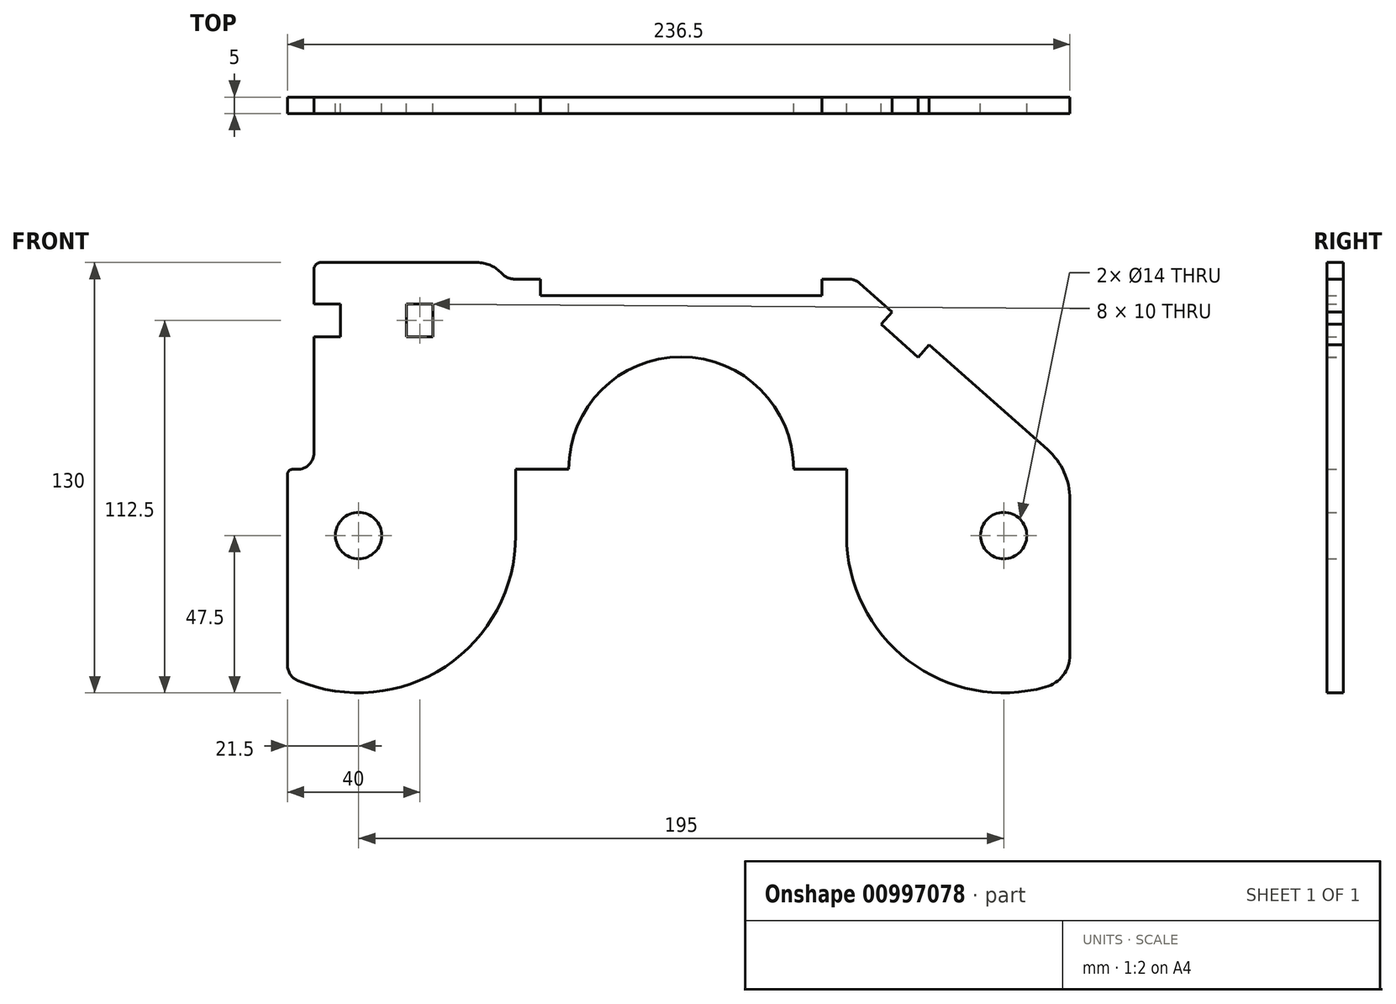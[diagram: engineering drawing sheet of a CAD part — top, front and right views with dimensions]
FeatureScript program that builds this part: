
annotation { "Feature Type Name" : "Feature", "Feature Type Description" : "" }
export const myFeature = defineFeature(function(context is Context, id is Id, definition is map)
    precondition{}
    {
        {
            var Q0;
            Q0=qCreatedBy(makeId("Front.planeOp"),FACE);
            var sketch = newSketch(context, id + "F0", { "sketchPlane" : qUnion([Q0])});
            skCircle(sketch, "E0", {"center": v(-97.5, -20) * mm, "radius": 7 * mm});
            skCircle(sketch, "E1", {"center": v(97.5, -20) * mm, "radius": 7 * mm});
            skArc(sketch, "E2", {"start": v(34, 0) * mm, "mid": v(0, 34) * mm, "end": v(-34, 0) * mm});
            skLineSegment(sketch, "E3", {"start": v(117.5, -9.01) * mm, "end": v(117.5, -56.14) * mm});
            skPoint(sketch, "E4.visualSharp", {"position": v(-34, 0) * mm});
            skPoint(sketch, "E5.visualSharp", {"position": v(34, 0) * mm});
            skPoint(sketch, "E6.visualSharp", {"position": v(117.5, 57.5) * mm});
            skLineSegment(sketch, "E7", {"start": v(-184.02, 45) * mm, "end": v(157.58, 45) * mm, "construction": true});
            skArc(sketch, "E8", {"start": v(-115.94, -63.77) * mm, "mid": v(-71.23, -59.57) * mm, "end": v(-50, -20) * mm});
            skArc(sketch, "E9", {"start": v(50, -20) * mm, "mid": v(68.74, -57.8) * mm, "end": v(110.17, -65.78) * mm});
            skLineSegment(sketch, "E10", {"start": v(-111, 60.5) * mm, "end": v(-111, 50) * mm});
            skPoint(sketch, "E11.visualSharp", {"position": v(-111, 0) * mm});
            skPoint(sketch, "E12.visualSharp", {"position": v(-111, 62.5) * mm});
            skLineSegment(sketch, "E13.bottom", {"start": v(-111, 50) * mm, "end": v(-103, 50) * mm});
            skLineSegment(sketch, "E13.top", {"start": v(-111, 40) * mm, "end": v(-103, 40) * mm});
            skLineSegment(sketch, "E13.right", {"start": v(-103, 50) * mm, "end": v(-103, 40) * mm});
            skLineSegment(sketch, "E14.bottom", {"start": v(-83, 50) * mm, "end": v(-75, 50) * mm});
            skLineSegment(sketch, "E14.top", {"start": v(-83, 40) * mm, "end": v(-75, 40) * mm});
            skLineSegment(sketch, "E14.left", {"start": v(-83, 50) * mm, "end": v(-83, 40) * mm});
            skLineSegment(sketch, "E14.right", {"start": v(-75, 50) * mm, "end": v(-75, 40) * mm});
            skPoint(sketch, "E15", {"position": v(-103, 45) * mm});
            skLineSegment(sketch, "E16.trimOffspring", {"start": v(-111, 40) * mm, "end": v(-111, 5) * mm});
            skLineSegment(sketch, "E17", {"start": v(-42.5, 57.5) * mm, "end": v(-42.5, 52.5) * mm});
            skLineSegment(sketch, "E18", {"start": v(-42.5, 52.5) * mm, "end": v(42.5, 52.5) * mm});
            skLineSegment(sketch, "E19", {"start": v(42.5, 52.5) * mm, "end": v(42.5, 57.5) * mm});
            skPoint(sketch, "E20", {"position": v(0, 52.5) * mm});
            skLineSegment(sketch, "E21.trimOffspring", {"start": v(42.5, 57.5) * mm, "end": v(50.6, 57.5) * mm});
            skLineSegment(sketch, "E22", {"start": v(-34, 0) * mm, "end": v(-50, 0) * mm});
            skLineSegment(sketch, "E23", {"start": v(-50, 0) * mm, "end": v(-50, -20) * mm});
            skLineSegment(sketch, "E24", {"start": v(34, 0) * mm, "end": v(50, 0) * mm});
            skLineSegment(sketch, "E25", {"start": v(50, 0) * mm, "end": v(50, -20) * mm});
            skPoint(sketch, "E26.visualSharp", {"position": v(-50, 0) * mm});
            skPoint(sketch, "E27.visualSharp", {"position": v(50, 0) * mm});
            skCircle(sketch, "E28", {"center": v(-97.5, -20) * mm, "radius": 40 * mm, "construction": true});
            skPoint(sketch, "E29.visualSharp", {"position": v(-111, -65.54) * mm});
            skPoint(sketch, "E30.visualSharp", {"position": v(117.5, -63.08) * mm});
            skArc(sketch, "E30.filletArc", {"start": v(110.17, -65.78) * mm, "mid": v(115.46, -62.2) * mm, "end": v(117.5, -56.14) * mm});
            skLineSegment(sketch, "E31", {"start": v(-109, 62.5) * mm, "end": v(-61.64, 62.5) * mm});
            skArc(sketch, "E32.filletArc", {"start": v(-109, 62.5) * mm, "mid": v(-110.41, 61.91) * mm, "end": v(-111, 60.5) * mm});
            skPoint(sketch, "E33.visualSharp", {"position": v(-57.5, 62.5) * mm});
            skLineSegment(sketch, "E34", {"start": v(-54.57, 59.57) * mm, "end": v(-53.96, 58.96) * mm});
            skLineSegment(sketch, "E35", {"start": v(-50.43, 57.5) * mm, "end": v(-42.5, 57.5) * mm});
            skPoint(sketch, "E36.visualSharp", {"position": v(-52.5, 57.5) * mm});
            skArc(sketch, "E36.filletArc", {"start": v(-53.96, 58.96) * mm, "mid": v(-52.34, 57.88) * mm, "end": v(-50.43, 57.5) * mm});
            skArc(sketch, "E37.filletArc", {"start": v(-54.57, 59.57) * mm, "mid": v(-57.82, 61.74) * mm, "end": v(-61.64, 62.5) * mm});
            skLineSegment(sketch, "E38", {"start": v(-119, -1.5) * mm, "end": v(-119, -59.17) * mm});
            skLineSegment(sketch, "E39", {"start": v(-117.5, 0) * mm, "end": v(-116, 0) * mm});
            skPoint(sketch, "E40.start.orphan", {"position": v(-119, -65.54) * mm});
            skPoint(sketch, "E41.visualSharp", {"position": v(-119, -62.36) * mm});
            skArc(sketch, "E41.filletArc", {"start": v(-119, -59.17) * mm, "mid": v(-118.17, -61.93) * mm, "end": v(-115.94, -63.77) * mm});
            skLineSegment(sketch, "E42.trimOffspring", {"start": v(-111, -57.65) * mm, "end": v(-111, -61.64) * mm});
            skArc(sketch, "E43.filletArc", {"start": v(-116, 0) * mm, "mid": v(-112.46, 1.46) * mm, "end": v(-111, 5) * mm});
            skPoint(sketch, "E44.visualSharp", {"position": v(-119, 0) * mm});
            skArc(sketch, "E44.filletArc", {"start": v(-117.5, 0) * mm, "mid": v(-118.56, -0.44) * mm, "end": v(-119, -1.5) * mm});
            skLineSegment(sketch, "E45", {"start": v(53.92, 56.24) * mm, "end": v(63.73, 47.56) * mm});
            skPoint(sketch, "E46.visualSharp", {"position": v(117.5, 0) * mm});
            skArc(sketch, "E46.filletArc", {"start": v(117.5, -9.01) * mm, "mid": v(115.73, -0.8) * mm, "end": v(110.75, 5.97) * mm});
            skPoint(sketch, "E47.visualSharp", {"position": v(52.5, 57.5) * mm});
            skArc(sketch, "E47.filletArc", {"start": v(53.92, 56.24) * mm, "mid": v(52.38, 57.18) * mm, "end": v(50.6, 57.5) * mm});
            skLineSegment(sketch, "E48", {"start": v(63.73, 47.56) * mm, "end": v(60.42, 43.82) * mm});
            skLineSegment(sketch, "E49", {"start": v(60.42, 43.82) * mm, "end": v(71.66, 33.88) * mm});
            skLineSegment(sketch, "E50", {"start": v(71.66, 33.88) * mm, "end": v(74.97, 37.62) * mm});
            skPoint(sketch, "E51", {"position": v(66.04, 38.85) * mm});
            skLineSegment(sketch, "E52.trimOffspring", {"start": v(74.97, 37.62) * mm, "end": v(110.75, 5.97) * mm});
            skSolve(sketch);
        }
        {
            var Q0;
            Q0 = qSketchRegion(id + "F0", true);
            extrude(context, id + "F1", {"entities" : qUnion([Q0]), "depth" : 5 * mm, "offsetDistance" : 25 * mm});
        }
    });
